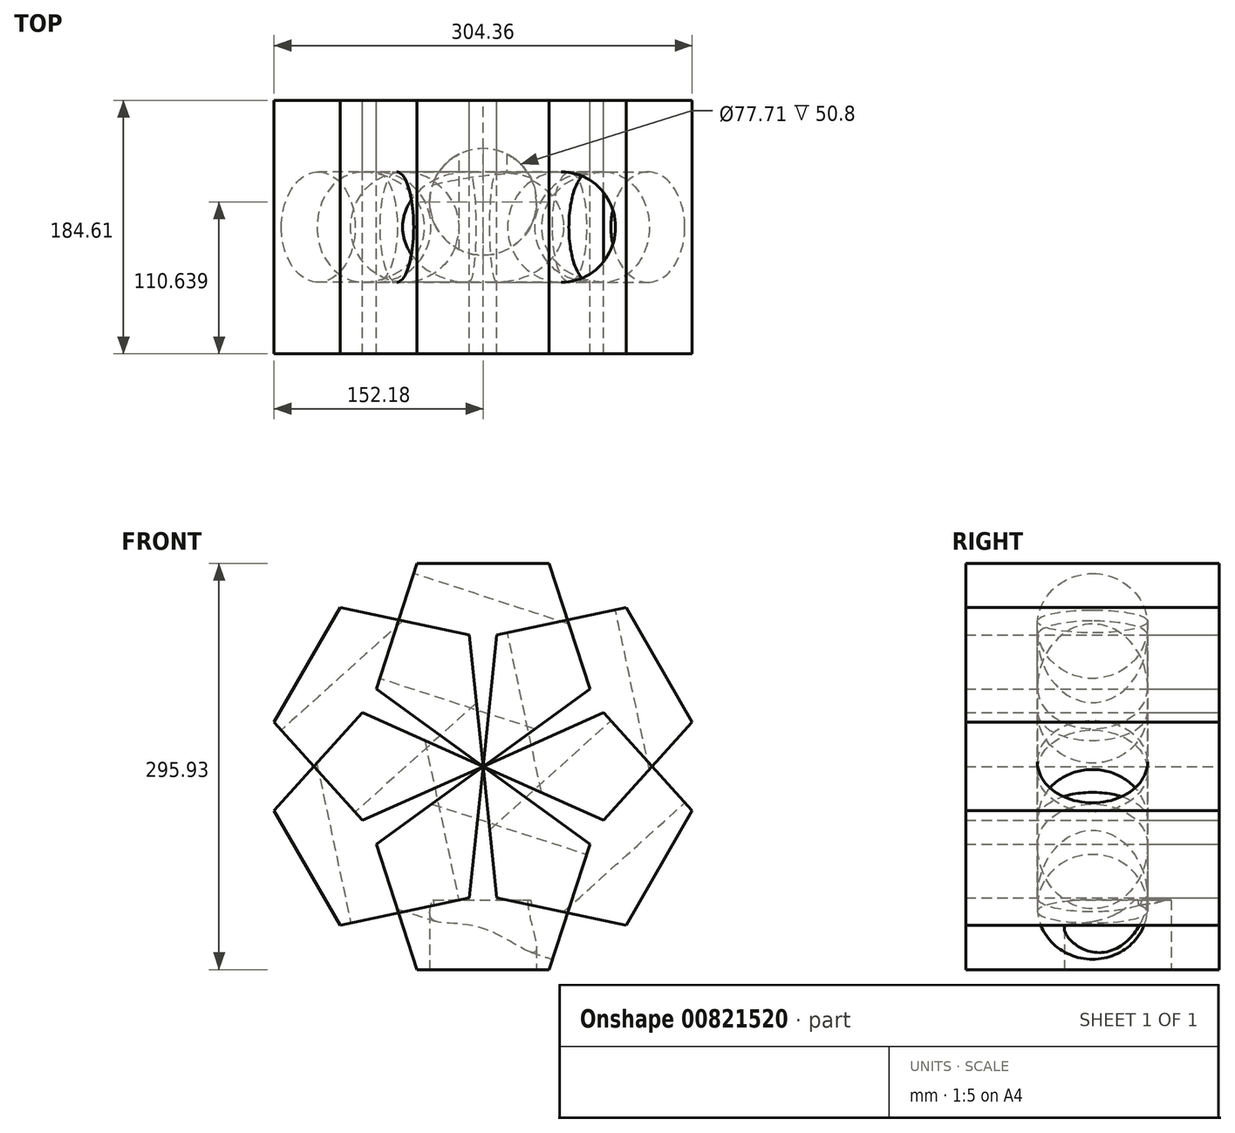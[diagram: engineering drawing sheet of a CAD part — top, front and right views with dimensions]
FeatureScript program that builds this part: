
annotation { "Feature Type Name" : "Feature", "Feature Type Description" : "" }
export const myFeature = defineFeature(function(context is Context, id is Id, definition is map)
    precondition{}
    {
        {
            var Q0;
            Q0=qCreatedBy(makeId("Front.planeOp"),FACE);
            var sketch = newSketch(context, id + "F0", { "sketchPlane" : qUnion([Q0])});
            skCircle(sketch, "E0.cCircle", {"center": v(0, 0) * mm, "radius": 66.17 * mm, "construction": true});
            skLineSegment(sketch, "E0.0", {"start": v(48.08, -66.17) * mm, "end": v(-48.08, -66.17) * mm});
            skLineSegment(sketch, "E0.1", {"start": v(-48.08, -66.17) * mm, "end": v(-77.8, 25.28) * mm});
            skLineSegment(sketch, "E0.2", {"start": v(-77.8, 25.28) * mm, "end": v(0, 81.8) * mm});
            skLineSegment(sketch, "E0.3", {"start": v(0, 81.8) * mm, "end": v(77.8, 25.28) * mm});
            skLineSegment(sketch, "E0.4", {"start": v(77.8, 25.28) * mm, "end": v(48.08, -66.17) * mm});
            skPoint(sketch, "E0.0.midPoint", {"position": v(0, -66.17) * mm});
            skSolve(sketch);
        }
        {
            var Q0;
            Q0=makeQuery(id+"F0.imprint","IMPRINT",FACE,{"disambiguationData":[TD([[makeQuery(id+"F0.imprint","IMPRINT",EDGE,{"derivedFrom":sQuery(id+"F0.wireOp",EDGE,"E0.0")}),-1.0]])]});
            extrude(context, id + "F1", {"entities" : qUnion([Q0]), "depth" : 184.6 * mm, "offsetDistance" : 25.4 * mm});
        }
        {
            var Q0;
            Q0=makeQuery(id+"F1.opExtrude","SWEPT_FACE",FACE,{"disambiguationData":[OSD([sQuery(id+"F0.wireOp",EDGE,"E0.4")])]});
            var sketch = newSketch(context, id + "F2", { "sketchPlane" : qUnion([Q0])});
            skCircle(sketch, "E1", {"center": v(-92.3, 0) * mm, "radius": 40.18 * mm});
            skPoint(sketch, "E1.centerSnap0", {"position": v(-92.3, 48.08) * mm});
            skSolve(sketch);
        }
        {
            var Q0;
            Q0 = qSketchRegion(id + "F2", true);
            extrude(context, id + "F3", {"entities" : qUnion([Q0]), "operationType" : NewBodyOperationType.REMOVE, "endBound" : BoundingType.UP_TO_NEXT, "oppositeDirection" : true, "depth" : 25.4 * mm, "offsetDistance" : 25.4 * mm});
        }
        {
            var Q0;
            Q0=makeQuery(id+"F1.opExtrude","SWEPT_BODY",BODY,{"disambiguationData":[OSD([sQuery(id+"F0.wireOp",EDGE,"E0.0"),sQuery(id+"F0.wireOp",EDGE,"E0.1"),sQuery(id+"F0.wireOp",EDGE,"E0.2"),sQuery(id+"F0.wireOp",EDGE,"E0.3"),sQuery(id+"F0.wireOp",EDGE,"E0.4")])]});
            var Q1;
            Q1=makeQuery(id+"F1.opExtrude","SWEPT_EDGE",EDGE,{"disambiguationData":[OSD([sQuery(id+"F0.wireOp",EDGE,"E0.2"),sQuery(id+"F0.wireOp",EDGE,"E0.3")])]});
            circularPattern(context, id + "F4", {"entities" : qUnion([Q0]), "axis" : qUnion([Q1]), "angle" : 360 * degree, "instanceCount" : 6, "equalSpace" : true});
        }
        {
            var Q0;
            Q0=makeQuery(id+"F1.opExtrude","SWEPT_FACE",FACE,{"disambiguationData":[OSD([sQuery(id+"F0.wireOp",EDGE,"E0.0")])]});
            var sketch = newSketch(context, id + "F5", { "sketchPlane" : qUnion([Q0])});
            skCircle(sketch, "E2", {"center": v(0, 73.97) * mm, "radius": 38.85 * mm});
            skSolve(sketch);
        }
        {
            var Q0;
            Q0=makeQuery(id+"F5.imprint","IMPRINT",FACE,{"disambiguationData":[TD([[makeQuery(id+"F5.imprint","IMPRINT",EDGE,{"derivedFrom":sQuery(id+"F5.wireOp",EDGE,"E2")}),1.0]])]});
            extrude(context, id + "F6", {"entities" : qUnion([Q0]), "operationType" : NewBodyOperationType.REMOVE, "oppositeDirection" : true, "depth" : 50.8 * mm, "offsetDistance" : 25.4 * mm});
        }
    });
